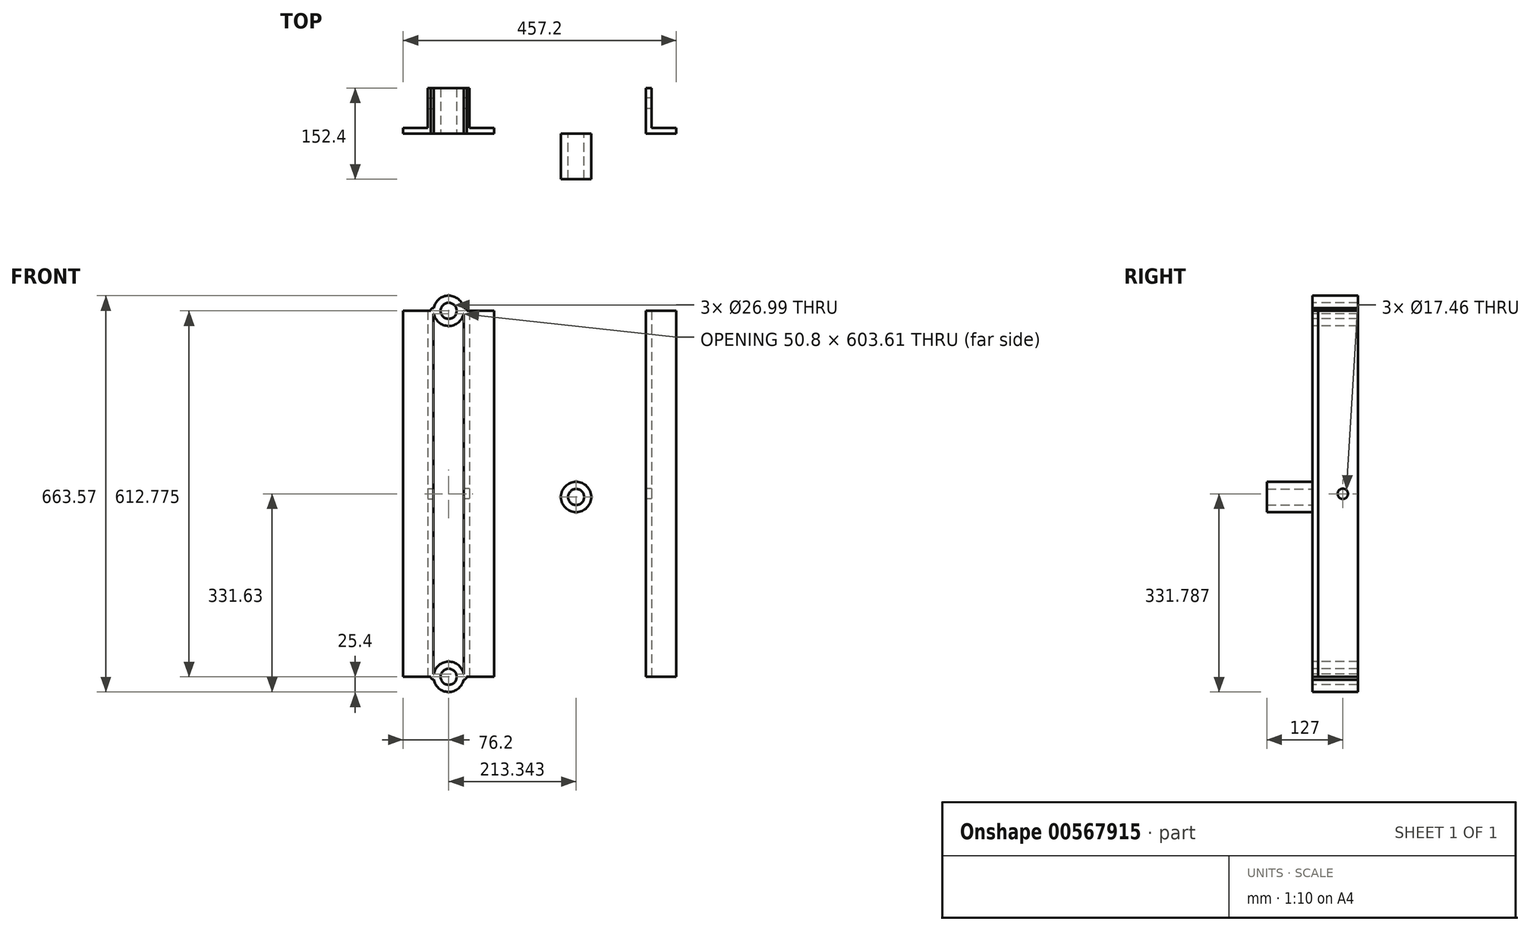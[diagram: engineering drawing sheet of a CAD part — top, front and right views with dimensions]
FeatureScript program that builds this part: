
annotation { "Feature Type Name" : "Feature", "Feature Type Description" : "" }
export const myFeature = defineFeature(function(context is Context, id is Id, definition is map)
    precondition{}
    {
        {
            var Q0;
            Q0=qCreatedBy(makeId("Top.planeOp"),FACE);
            var sketch = newSketch(context, id + "F0", { "sketchPlane" : qUnion([Q0])});
            skLineSegment(sketch, "E0", {"start": v(0, 0) * mm, "end": v(-50.8, 0) * mm});
            skLineSegment(sketch, "E1", {"start": v(-50.8, 0) * mm, "end": v(-50.8, 76.2) * mm});
            skLineSegment(sketch, "E2", {"start": v(-50.8, 76.2) * mm, "end": v(-41.28, 76.2) * mm});
            skLineSegment(sketch, "E3", {"start": v(0, 0) * mm, "end": v(0, 9.53) * mm});
            skLineSegment(sketch, "E4", {"start": v(-41.28, 76.2) * mm, "end": v(-41.28, 9.52) * mm});
            skLineSegment(sketch, "E5", {"start": v(-41.28, 9.52) * mm, "end": v(0, 9.52) * mm});
            skSolve(sketch);
        }
        {
            var Q0;
            Q0=makeQuery(id+"F0.imprint","IMPRINT",FACE,{"disambiguationData":[TD([[makeQuery(id+"F0.imprint","IMPRINT",EDGE,{"derivedFrom":sQuery(id+"F0.wireOp",EDGE,"E0")}),-1.0]])]});
            extrude(context, id + "F1", {"entities" : qUnion([Q0]), "depth" : 612.77 * mm});
        }
        {
            var Q0;
            Q0=makeQuery(id+"F1.opExtrude","SWEPT_FACE",FACE,{"disambiguationData":[OSD([sQuery(id+"F0.wireOp",EDGE,"E4")])]});
            var sketch = newSketch(context, id + "F2", { "sketchPlane" : qUnion([Q0])});
            skPoint(sketch, "E6", {"position": v(50.8, 306.39) * mm});
            skPoint(sketch, "E6.positionSnap0", {"position": v(76.2, 306.39) * mm});
            skSolve(sketch);
        }
        {
            var Q0;
            Q0=sQuery(id+"F2.wireOp",VERTEX,"E6");
            var Q1;
            Q1=makeQuery(id+"F1.opExtrude","SWEPT_BODY",BODY,{"disambiguationData":[OSD([sQuery(id+"F0.wireOp",EDGE,"E0"),sQuery(id+"F0.wireOp",EDGE,"E1"),sQuery(id+"F0.wireOp",EDGE,"E2"),sQuery(id+"F0.wireOp",EDGE,"E3"),sQuery(id+"F0.wireOp",EDGE,"E4"),sQuery(id+"F0.wireOp",EDGE,"E5")])]});
            hole(context, id + "F3", {"style" : HoleStyle.SIMPLE, "endStyle" : HoleEndStyle.THROUGH, "holeDiameter" : 17.46 * mm, "locations" : qUnion([Q0]), "scope" : qUnion([Q1]), "isTappedThrough" : true});
        }
        {
            var Q0;
            Q0=makeQuery(id+"F1.opExtrude","SWEPT_FACE",FACE,{"disambiguationData":[OSD([sQuery(id+"F0.wireOp",EDGE,"E0")])]});
            var sketch = newSketch(context, id + "F4", { "sketchPlane" : qUnion([Q0])});
            skCircle(sketch, "E7", {"center": v(137.14, 301.06) * mm, "radius": 25.4 * mm});
            skCircle(sketch, "E8", {"center": v(137.14, 301.06) * mm, "radius": 13.5 * mm});
            skLineSegment(sketch, "E9", {"start": v(111.74, 301.06) * mm, "end": v(162.54, 301.06) * mm});
            skLineSegment(sketch, "E10", {"start": v(137.14, 326.46) * mm, "end": v(137.14, 275.66) * mm});
            skLineSegment(sketch, "E11", {"start": v(-50.8, 306.39) * mm, "end": v(-134.77, 306.39) * mm});
            skLineSegment(sketch, "E12.0", {"start": v(-50.8, 0) * mm, "end": v(-134.77, 0) * mm});
            skLineSegment(sketch, "E13.0", {"start": v(-50.8, 612.78) * mm, "end": v(-134.77, 612.78) * mm});
            skLineSegment(sketch, "E14", {"start": v(-50.8, 612.78) * mm, "end": v(-50.8, 0) * mm});
            skLineSegment(sketch, "E15.0", {"start": v(-76.2, 612.78) * mm, "end": v(-76.2, 0) * mm});
            skCircle(sketch, "E16", {"center": v(-76.2, 612.78) * mm, "radius": 25.4 * mm});
            skCircle(sketch, "E17", {"center": v(-76.2, 612.78) * mm, "radius": 13.5 * mm});
            skCircle(sketch, "E18", {"center": v(-76.2, 0) * mm, "radius": 25.4 * mm});
            skCircle(sketch, "E19", {"center": v(-76.2, 0) * mm, "radius": 13.5 * mm});
            skPoint(sketch, "E20.centerSnap0", {"position": v(-92.79, 0) * mm});
            skSolve(sketch);
        }
        {
            var Q0;
            Q0=makeQuery(id+"F4.imprint","IMPRINT",FACE,{"disambiguationData":[TD([[makeQuery(id+"F4.imprint","IMPRINT",EDGE,{"derivedFrom":sQuery(id+"F4.wireOp",EDGE,"E7")}),1.0]])]});
            extrude(context, id + "F5", {"entities" : qUnion([Q0]), "depth" : 76.2 * mm});
        }
        {
            var Q0;
            {var subQ0=sQuery(id+"F4.wireOp",EDGE,"E18");var subQ1=sQuery(id+"F4.wireOp",EDGE,"E12.0");var subQ5=makeQuery(id+"F4.imprint","INTERSECT",VERTEX,{"derivedFrom":[subQ1,subQ0]});Q0=makeQuery(id+"F4.imprint","IMPRINT",FACE,{"disambiguationData":[TD([[makeQuery(id+"F4.imprint","IMPRINT",EDGE,{"disambiguationData":[TD([[subQ5,1.0]])],"derivedFrom":subQ1}),1.0]])]});}
            var Q1;
            {var subQ0=sQuery(id+"F4.wireOp",EDGE,"E18");var subQ1=sQuery(id+"F4.wireOp",EDGE,"E12.0");var subQ2=makeQuery(id+"F4.imprint","INTERSECT",VERTEX,{"derivedFrom":[subQ1,subQ0]});Q1=makeQuery(id+"F4.imprint","IMPRINT",FACE,{"disambiguationData":[TD([[makeQuery(id+"F4.imprint","IMPRINT",EDGE,{"disambiguationData":[TD([[subQ2,1.0]])],"derivedFrom":subQ1}),-1.0]])]});}
            var Q2;
            {var subQ0=sQuery(id+"F4.wireOp",EDGE,"E18");var subQ5=sQuery(id+"F4.wireOp",EDGE,"E15.0");var subQ6=makeQuery(id+"F4.imprint","INTERSECT",VERTEX,{"derivedFrom":[subQ5,subQ0]});Q2=makeQuery(id+"F4.imprint","IMPRINT",FACE,{"disambiguationData":[TD([[makeQuery(id+"F4.imprint","IMPRINT",EDGE,{"disambiguationData":[TD([[subQ6,-1.0]])],"derivedFrom":subQ5}),1.0]])]});}
            var Q3;
            {var subQ0=sQuery(id+"F4.wireOp",EDGE,"E16");var subQ1=sQuery(id+"F4.wireOp",EDGE,"E13.0");var subQ2=makeQuery(id+"F4.imprint","INTERSECT",VERTEX,{"derivedFrom":[subQ1,subQ0]});Q3=makeQuery(id+"F4.imprint","IMPRINT",FACE,{"disambiguationData":[TD([[makeQuery(id+"F4.imprint","IMPRINT",EDGE,{"disambiguationData":[TD([[subQ2,1.0]])],"derivedFrom":subQ1}),1.0]])]});}
            var Q4;
            {var subQ0=sQuery(id+"F4.wireOp",EDGE,"E16");var subQ5=sQuery(id+"F4.wireOp",EDGE,"E15.0");var subQ7=makeQuery(id+"F4.imprint","INTERSECT",VERTEX,{"derivedFrom":[subQ5,subQ0]});Q4=makeQuery(id+"F4.imprint","IMPRINT",FACE,{"disambiguationData":[TD([[makeQuery(id+"F4.imprint","IMPRINT",EDGE,{"disambiguationData":[TD([[subQ7,1.0]])],"derivedFrom":subQ5}),1.0]])]});}
            var Q5;
            {var subQ0=sQuery(id+"F4.wireOp",EDGE,"E16");var subQ1=sQuery(id+"F4.wireOp",EDGE,"E13.0");var subQ5=makeQuery(id+"F4.imprint","INTERSECT",VERTEX,{"derivedFrom":[subQ1,subQ0]});Q5=makeQuery(id+"F4.imprint","IMPRINT",FACE,{"disambiguationData":[TD([[makeQuery(id+"F4.imprint","IMPRINT",EDGE,{"disambiguationData":[TD([[subQ5,1.0]])],"derivedFrom":subQ1}),-1.0]])]});}
            extrude(context, id + "F6", {"entities" : qUnion([Q0, Q1, Q2, Q3, Q4, Q5]), "oppositeDirection" : true, "depth" : 76.2 * mm});
        }
        {
            var Q0;
            Q0=makeQuery(id+"F1.opExtrude","SWEPT_BODY",BODY,{"disambiguationData":[OSD([sQuery(id+"F0.wireOp",EDGE,"E0"),sQuery(id+"F0.wireOp",EDGE,"E1"),sQuery(id+"F0.wireOp",EDGE,"E2"),sQuery(id+"F0.wireOp",EDGE,"E3"),sQuery(id+"F0.wireOp",EDGE,"E4"),sQuery(id+"F0.wireOp",EDGE,"E5")])]});
            transform(context, id + "F7", {"entities" : qUnion([Q0]), "transformType" : TransformType.TRANSLATION_3D, "dx" : 304.8 * mm, "dy" : 0 * mm, "dz" : 0 * mm, "makeCopy" : true});
        }
        {
            var Q0;
            Q0=qCreatedBy(makeId("Right.planeOp"),FACE);
            cPlane(context, id + "F8", {"entities" : qUnion([Q0]), "cplaneType" : CPlaneType.OFFSET, "offset" : 76.2 * mm, "oppositeDirection" : true, "width" : 152.4 * mm, "height" : 152.4 * mm});
        }
        {
            var Q0;
            Q0=makeQuery(id+"F1.opExtrude","SWEPT_BODY",BODY,{"disambiguationData":[OSD([sQuery(id+"F0.wireOp",EDGE,"E0"),sQuery(id+"F0.wireOp",EDGE,"E1"),sQuery(id+"F0.wireOp",EDGE,"E2"),sQuery(id+"F0.wireOp",EDGE,"E3"),sQuery(id+"F0.wireOp",EDGE,"E4"),sQuery(id+"F0.wireOp",EDGE,"E5")])]});
            var Q1;
            Q1=qCreatedBy(id+"F8.planeOp",FACE);
            mirror(context, id + "F9", {"entities" : qUnion([Q0]), "mirrorPlane" : qUnion([Q1])});
        }
        {
            var Q0;
            {var subQ0=sQuery(id+"F4.wireOp",EDGE,"E16");var subQ1=sQuery(id+"F4.wireOp",EDGE,"E13.0");var subQ5=makeQuery(id+"F4.imprint","INTERSECT",VERTEX,{"derivedFrom":[subQ1,subQ0]});Q0=makeQuery(id+"F4.imprint","IMPRINT",FACE,{"disambiguationData":[TD([[makeQuery(id+"F4.imprint","IMPRINT",EDGE,{"disambiguationData":[TD([[subQ5,1.0]])],"derivedFrom":subQ1}),-1.0]])]});}
            var sketch = newSketch(context, id + "F10", { "sketchPlane" : qUnion([Q0])});
            skCircle(sketch, "E21", {"center": v(-101.6, 612.78) * mm, "radius": 4.76 * mm});
            skSolve(sketch);
        }
        {
            var Q0;
            {var subQ0=sQuery(id+"F0.wireOp",EDGE,"E0");var subQ1=makeQuery(id+"F1.opExtrude","CAP_EDGE",EDGE,{"disambiguationData":[OSD([subQ0])],"isStart":true});Q0=makeQuery(id+"F4.imprint","IMPRINT",FACE,{"disambiguationData":[TD([[makeQuery(id+"F4.imprint","IMPRINT",EDGE,{"derivedFrom":subQ1}),-1.0]])]});}
            var sketch = newSketch(context, id + "F11", { "sketchPlane" : qUnion([Q0])});
            skCircle(sketch, "E22", {"center": v(-50.6, 612.66) * mm, "radius": 4.76 * mm});
            skSolve(sketch);
        }
        {
            var Q0;
            {var subQ0=sQuery(id+"F4.wireOp",EDGE,"E16");var subQ1=sQuery(id+"F4.wireOp",EDGE,"E13.0");var subQ2=makeQuery(id+"F4.imprint","INTERSECT",VERTEX,{"derivedFrom":[subQ1,subQ0]});Q0=makeQuery(id+"F4.imprint","IMPRINT",FACE,{"disambiguationData":[TD([[makeQuery(id+"F4.imprint","IMPRINT",EDGE,{"disambiguationData":[TD([[subQ2,1.0]])],"derivedFrom":subQ1}),1.0]])]});}
            var sketch = newSketch(context, id + "F12", { "sketchPlane" : qUnion([Q0])});
            skCircle(sketch, "E23", {"center": v(-101.64, 0) * mm, "radius": 4.45 * mm});
            skSolve(sketch);
        }
        {
            var Q0;
            {var subQ0=sQuery(id+"F0.wireOp",EDGE,"E0");var subQ1=makeQuery(id+"F1.opExtrude","CAP_EDGE",EDGE,{"disambiguationData":[OSD([subQ0])],"isStart":true});Q0=makeQuery(id+"F4.imprint","IMPRINT",FACE,{"disambiguationData":[TD([[makeQuery(id+"F4.imprint","IMPRINT",EDGE,{"derivedFrom":subQ1}),-1.0]])]});}
            var sketch = newSketch(context, id + "F13", { "sketchPlane" : qUnion([Q0])});
            skCircle(sketch, "E24", {"center": v(-50.93, 0) * mm, "radius": 4.77 * mm});
            skSolve(sketch);
        }
        {
            var Q0;
            {var subQ0=sQuery(id+"F13.wireOp",EDGE,"E24");var subQ2=makeQuery(id+"F1.opExtrude","CAP_EDGE",EDGE,{"disambiguationData":[OSD([sQuery(id+"F0.wireOp",EDGE,"E0")])],"isStart":true});var subQ5=makeQuery(id+"F4.imprint","IMPRINT",EDGE,{"derivedFrom":subQ2});var subQ6=makeQuery(id+"F13.imprint","INTERSECT",VERTEX,{"derivedFrom":[subQ5,subQ0]});Q0=makeQuery(id+"F13.imprint","IMPRINT",FACE,{"disambiguationData":[TD([[makeQuery(id+"F13.imprint","IMPRINT",EDGE,{"disambiguationData":[TD([[subQ6,1.0]])],"derivedFrom":subQ0}),1.0]])]});}
            extrude(context, id + "F14", {"entities" : qUnion([Q0]), "operationType" : NewBodyOperationType.ADD, "oppositeDirection" : true, "depth" : 76.2 * mm});
        }
        {
            var Q0;
            Q0=makeQuery(id+"F12.imprint","IMPRINT",FACE,{"disambiguationData":[TD([[makeQuery(id+"F12.imprint","IMPRINT",EDGE,{"derivedFrom":sQuery(id+"F12.wireOp",EDGE,"E23")}),1.0]])]});
            var Q1;
            {var subQ0=sQuery(id+"F10.wireOp",EDGE,"E21");var subQ1=sQuery(id+"F4.wireOp",EDGE,"E16");var subQ2=sQuery(id+"F4.wireOp",EDGE,"E13.0");var subQ3=makeQuery(id+"F4.imprint","INTERSECT",VERTEX,{"derivedFrom":[subQ2,subQ1]});var subQ4=makeQuery(id+"F4.imprint","IMPRINT",EDGE,{"disambiguationData":[TD([[subQ3,1.0]])],"derivedFrom":subQ2});var subQ5=makeQuery(id+"F10.imprint","INTERSECT",VERTEX,{"derivedFrom":[subQ4,subQ0]});Q1=makeQuery(id+"F10.imprint","IMPRINT",FACE,{"disambiguationData":[TD([[makeQuery(id+"F10.imprint","IMPRINT",EDGE,{"disambiguationData":[TD([[subQ5,1.0]])],"derivedFrom":subQ0}),1.0]])]});}
            var Q2;
            {var subQ0=sQuery(id+"F11.wireOp",EDGE,"E22");var subQ2=makeQuery(id+"F1.opExtrude","CAP_EDGE",EDGE,{"disambiguationData":[OSD([sQuery(id+"F0.wireOp",EDGE,"E0")])],"isStart":false});var subQ5=makeQuery(id+"F4.imprint","IMPRINT",EDGE,{"derivedFrom":subQ2});var subQ6=makeQuery(id+"F11.imprint","INTERSECT",VERTEX,{"derivedFrom":[subQ5,subQ0]});Q2=makeQuery(id+"F11.imprint","IMPRINT",FACE,{"disambiguationData":[TD([[makeQuery(id+"F11.imprint","IMPRINT",EDGE,{"disambiguationData":[TD([[subQ6,-1.0]])],"derivedFrom":subQ0}),1.0]])]});}
            var Q3;
            Q3=sQuery(id+"F12.wireOp",EDGE,"E23");
            extrude(context, id + "F15", {"entities" : qUnion([Q0, Q1, Q2]), "operationType" : NewBodyOperationType.ADD, "surfaceEntities" : qUnion([Q3]), "oppositeDirection" : true, "depth" : 76.2 * mm});
        }
    });
